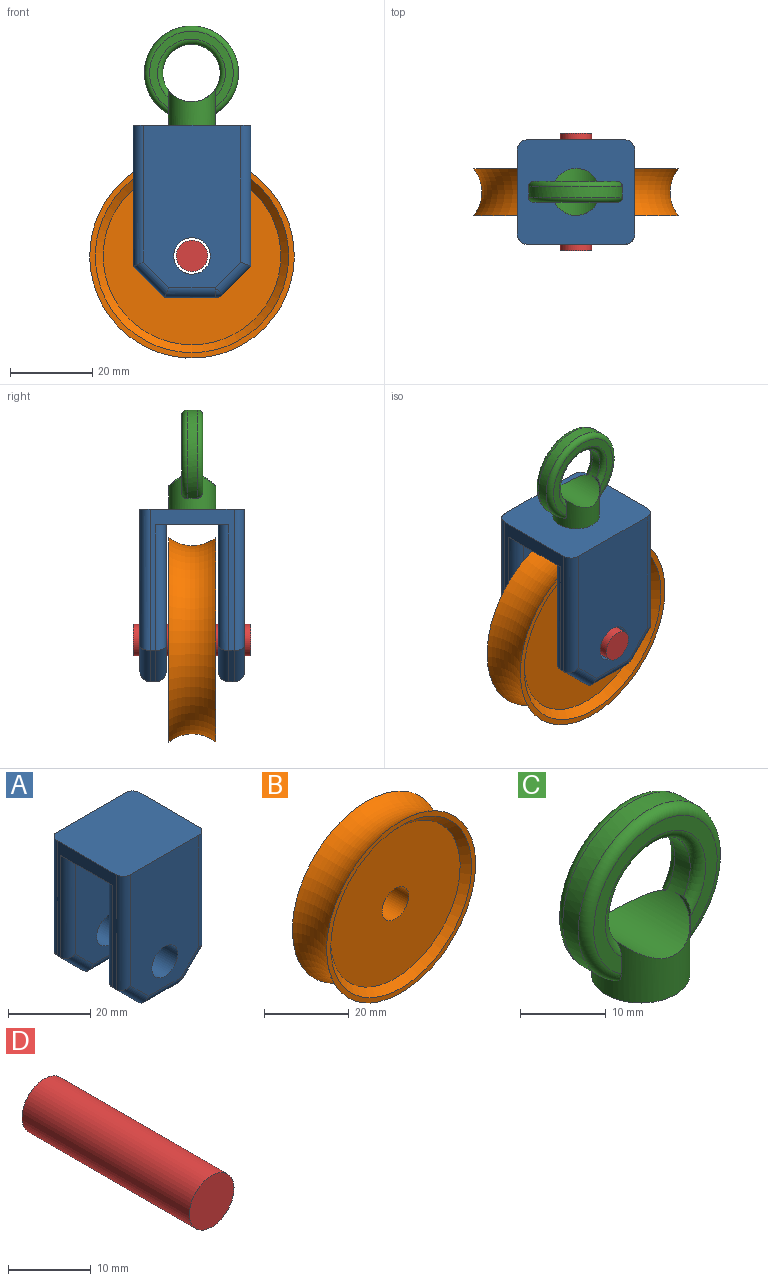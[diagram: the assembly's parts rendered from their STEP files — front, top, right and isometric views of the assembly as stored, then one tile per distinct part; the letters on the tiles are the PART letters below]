
ASSEMBLY  parts=4 mates=3
PART A: 40 faces, bbox 30.4x25.4x41.9 mm
  f0: plane 34.29x20.32mm, normal (1,0,0), area 305.8mm2, adj f5,f6,f7,f9,f10,f11,f25,f26
  f1: plane 34.29x20.32mm, normal (-1,0,0), area 154.8mm2, adj f10,f11,f12,f13,f17,f30,f31,f35
  f2: cylinder r=4.45mm len=8.89mm, axis (0,1,0), area 177.3mm2, adj f4,f5
  f3: plane 12.28x1.27mm, normal (0,0,-1), area 15.6mm2, adj f12,f15,f18,f21
  f4: plane 39.37x23.5mm, normal (0,-1,0), area 825.3mm2, adj f2,f7,f8,f10,f13,f14,f15
  f5: plane 35.56x26.04mm, normal (0,1,0), area 807.3mm2, adj f0,f2,f9,f11,f17,f19,f21
  f6: plane 6.88x6.88mm, normal (0.71,0,-0.71), area 12.3mm2, adj f0,f8,f9,f18
  f7: cylinder r=2.54mm len=34.29mm, axis (0,0,-1), area 135.3mm2, adj f0,f4,f8,f10
  f8: cylinder r=2.54mm len=8.67mm, axis (0.71,0,0.71), area 37.3mm2, adj f4,f6,f7,f16
  f9: cylinder r=2.54mm len=10.47mm, axis (0.71,0,0.71), area 42.5mm2, adj f0,f5,f6,f20
  f10: plane 28.58x25.4mm, normal (0,0,1), area 720.3mm2, adj f0,f1,f4,f7,f13,f24,f27,f31
  f11: plane 28.58x17.78mm, normal (0,0,-1), area 365.7mm2, adj f0,f1,f5,f17,f25,f35
  f12: plane 7.62x7.62mm, normal (-0.71,0,-0.71), area 13.7mm2, adj f1,f3,f14,f19
  f13: cylinder r=2.54mm len=34.29mm, axis (0,0,1), area 135.3mm2, adj f1,f4,f10,f14
  f14: cylinder r=2.54mm len=9.42mm, axis (0.71,0,-0.71), area 39.9mm2, adj f4,f12,f13,f15
  f15: cylinder r=2.54mm len=12.28mm, axis (-1,0,0), area 47.5mm2, adj f3,f4,f14,f16
  f16: sphere r=2.54mm, area 5.1mm2, adj f8,f15,f18
  f17: cylinder r=2.54mm len=30.48mm, axis (0,0,-1), area 120.1mm2, adj f1,f5,f11,f19
  f18: cylinder r=2.54mm len=1.8mm, axis (0,1,0), area 2.5mm2, adj f3,f6,f16,f20
  f19: cylinder r=2.54mm len=9.42mm, axis (0.71,0,-0.71), area 39.9mm2, adj f5,f12,f17,f21
  f20: sphere r=2.54mm, area 5.1mm2, adj f9,f18,f21
  f21: cylinder r=2.54mm len=12.28mm, axis (1,0,0), area 47.5mm2, adj f3,f5,f19,f20
  f22: cylinder r=4.45mm len=8.89mm, axis (0,-1,0), area 177.3mm2, adj f24,f25
  f23: plane 12.28x1.27mm, normal (0,0,-1), area 15.6mm2, adj f30,f33,f36,f39
  f24: plane 39.37x23.5mm, normal (0,1,0), area 825.3mm2, adj f10,f22,f27,f28,f31,f32,f33
  f25: plane 35.56x26.04mm, normal (0,-1,0), area 807.3mm2, adj f0,f11,f22,f29,f35,f37,f39
  f26: plane 6.88x6.88mm, normal (0.71,0,-0.71), area 12.3mm2, adj f0,f28,f29,f36
  f27: cylinder r=2.54mm len=34.29mm, axis (0,0,-1), area 135.3mm2, adj f0,f10,f24,f28
  f28: cylinder r=2.54mm len=8.67mm, axis (0.71,0,0.71), area 37.3mm2, adj f24,f26,f27,f34
  f29: cylinder r=2.54mm len=10.47mm, axis (0.71,0,0.71), area 42.5mm2, adj f0,f25,f26,f38
  f30: plane 7.62x7.62mm, normal (-0.71,0,-0.71), area 13.7mm2, adj f1,f23,f32,f37
  f31: cylinder r=2.54mm len=34.29mm, axis (0,0,1), area 135.3mm2, adj f1,f10,f24,f32
  f32: cylinder r=2.54mm len=9.42mm, axis (0.71,0,-0.71), area 39.9mm2, adj f24,f30,f31,f33
  f33: cylinder r=2.54mm len=12.28mm, axis (-1,0,0), area 47.5mm2, adj f23,f24,f32,f34
  f34: sphere r=2.54mm, area 5.1mm2, adj f28,f33,f36
  f35: cylinder r=2.54mm len=30.48mm, axis (0,0,-1), area 120.1mm2, adj f1,f11,f25,f37
  f36: cylinder r=2.54mm len=1.8mm, axis (0,-1,0), area 2.5mm2, adj f23,f26,f34,f38
  f37: cylinder r=2.54mm len=9.42mm, axis (0.71,0,-0.71), area 39.9mm2, adj f25,f30,f35,f39
  f38: sphere r=2.54mm, area 5.1mm2, adj f29,f36,f39
  f39: cylinder r=2.54mm len=12.28mm, axis (1,0,0), area 47.5mm2, adj f23,f25,f37,f38
PART B: 8 faces, bbox 55.3x13.1x55.3 mm
  f0: plane 49.7x49.7mm, normal (0,-1,0), area 205.5mm2, adj f6,f7
  f1: plane 49.7x49.7mm, normal (0,1,0), area 205.5mm2, adj f5,f7
  f2: cylinder r=4.45mm len=8.89mm, axis (0,1,0), area 212.8mm2, adj f3,f4
  f3: plane 43.18x43.18mm, normal (0,-1,0), area 1402.3mm2, adj f2,f6
  f4: plane 43.18x43.18mm, normal (0,1,0), area 1402.3mm2, adj f2,f5
  f5: cone r=23.49mm half-angle=45deg, axis (0,1,0), area 381.6mm2, adj f1,f4
  f6: cone r=21.59mm half-angle=45deg, axis (0,-1,0), area 381.6mm2, adj f0,f3
  f7: torus R=32.07mm, axis (0,1,0), area 1823.3mm2, adj f0,f1
PART C: 13 faces, bbox 20000000000000000038313501714693374724319102545303840223056070291987586484079775119224722902163606470656x20000000000000000038313501714693374724319102545303840223056070291987586484079775119224722902163606470656x20000000000000000038313501714693374724319102545303840223056070291987586484079775119224722902163606470656 mm
  f0: cylinder r=5.71mm len=11.43mm, axis (0,0,-1), area 226.7mm2, adj f1,f2,f3,f4,f8,f9,f10,f11
  f1: torus R=8.26mm, axis (0,1,0), area 69.7mm2, adj f0,f2,f9
  f2: plane 20.32x19.01mm, normal (0,1,0), area 89.5mm2, adj f0,f1,f3
  f3: torus R=10.16mm, axis (0,1,0), area 115.4mm2, adj f0,f2,f4
  f4: cylinder r=11.43mm len=22.86mm, axis (0,-1,0), area 152.2mm2, adj f0,f3,f5,f8,f10
  f5: torus R=10.16mm, axis (0,1,0), area 113.5mm2, adj f4,f6,f8,f10
  f6: plane 20.32x18.65mm, normal (0,-1,0), area 86.7mm2, adj f5,f7,f8,f10
  f7: torus R=8.26mm, axis (0,1,0), area 67.3mm2, adj f6,f8,f9,f10
  f8: plane 5.78x2.54mm, normal (1,0,0), area 13.7mm2, adj f0,f4,f5,f6,f7,f9
  f9: cylinder r=6.99mm len=13.97mm, axis (0,-1,0), area 192.4mm2, adj f0,f1,f7,f8,f10
  f10: plane 6x2.54mm, normal (-1,0,0), area 14.2mm2, adj f0,f4,f5,f6,f7,f9
  f11: plane 11.43x11.43mm, normal (0,0,-1), area 102.6mm2, adj f0
  f12: cylinder r=6.99mm len=20000000000000000038313501714693374724319102545303840223056070291987586484079775119224722902163606470656mm, axis (0,-1,0), area 558799999999999954600596027778069046798558458276849996845563873453962448728234915934315357035332554981376mm2
PART D: 3 faces, bbox 7.6x28.6x7.6 mm
  f0: cylinder r=3.81mm len=28.58mm, axis (0,1,0), area 684.1mm2, adj f1,f2
  f1: plane 7.62x7.62mm, normal (0,-1,0), area 45.6mm2, adj f0
  f2: plane 7.62x7.62mm, normal (0,1,0), area 45.6mm2, adj f0
PLACE A t=(0.29,-29.01,-3.51)mm
PLACE B t=(-14,-22.66,1.57)mm fixed
PLACE C t=(0.29,-29.01,-3.51)mm
PLACE D t=(-14,-8.31,1.57)mm
MATE cylindrical B.f7 <-> D.f0  axis (0,1,0) through (-14,-22.66,1.57)mm
MATE fastened A.f10 <-> C.f0  axis (0,0,1) through (-14,-22.66,33.32)mm
MATE slider A.f2 <-> D.f0  axis (0,-1,0) through (-14,-9.96,1.57)mm
